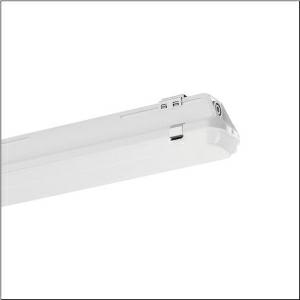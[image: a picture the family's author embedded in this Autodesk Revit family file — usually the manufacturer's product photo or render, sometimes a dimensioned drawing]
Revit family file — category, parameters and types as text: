
# Revit family: monsun_r__11_emergency_51fp207p437l3g_ce37
name_source: partatom
category: Lighting Fixtures
units: mm (PartAtom-declared; Revit-internal decimal feet)

## family parameters
Cut with Voids When Loaded = No
Host = Face
Light Source = No
Part Type = Normal
Room Calculation Point = No
Round Connector Dimension = Use Diameter
Shared = No

## types (1)
- --- (1 x LED, 890 lm, 6.4 W, 4000K)
    Apparent Load = 6 VA
    CIE Flux Codes = 45 75 93 94 100
    Color Rendering = 80
    Color Temperature = 4000K
    Default Elevation = 1800 mm
    Description = Monsun® 11 emergency, damp-proof luminaire, chain hanger, primary optical cover: enclosure, of PC, light emission: direct distribution, primary light characteristic: symmetric, installation type: suspended mounting, surface-mounted, horizontal mounting, vertical mounting, LED, rated luminous flux: 3.990lm, luminous efficacy: 164lm/W, light colour: 840, colour temperature: 4000K, control gear: ON/OFF, with terminal, 4-pole, max. 2.5mm², mains connection: 220..240V, AC, 50/60Hz, rated input power: 28W, control gear: single battery element, battery: LiFePO4, 9Ah, luminaire housing, of glass-fibre reinforced polyester, uncoated, bright grey, incl. chain hanger, length: 1.590mm, width: 90mm, height: 88mm, clip for enclosure, of stainless steel (V2A), ceiling mounting element, of stainless steel (V2A), chain hanger, of stainless steel (V2A), protection rating (complete): IP66, insulation class (complete): insulation class I (protective earthing), certification: CE, UKCA, protection symbol: D, impact resistance: IK08, permissible operating ambient temperature: +5..+35°C, standard: EN 50419, EN 60598-2-1, EN 60598-2-22, contact your sales advisor before using the luminaires in applications with unclear chemical exposure, large temperature fluctuations or condensation-forming humidity, LABS conformity tested according to VDMA 24364:2018-05, no direct snow, no direct sun, no direct rain, for indoor or canopied outdoor use, corresponds to IFS (International Featured Standards) requirements for safety and quality in the food industry, packaging unit: 1 piece
    Height = 89 mm
    Lamp = 1 x LED
    Lamp Light Flux = 890 lm
    Lamp Power = 6.4 W
    Lamp count = 1
    Length = 1590 mm
    Luminous efficacy = 139 lm/W
    Manufacturer = Siteco
    ModVariant = No
    Model = 51FP207P437L3G
    Mounting Place = Ceiling
    Mounting Type = Surface mounted
    Number of Poles = 1
    OnlyDefault = Yes
    Power Factor = 1
    Product Name = Monsun® 11 emergency
    Product group = damp-proof luminaire
    ProductGroupID = 300
    Protection Class = Protection class I
    Protection Degree = IP 66
    RLX_Detail_Level = 1
    RLX_Emergency_Light_Flux = 0 lm
    RLX_Emergency_Type = 0
    RLX_Emergency_Type_DB = No
    RlxData = <blob elided: 88681 chars, md5=a2ae6787>
    Socket = socket
    Standby Power = 0 W
    System Light Flux = 890 lm
    System Power = 6 W
    Type Comments = : emergency light operation: 3 h
    Type Image = l_1349237.jpg
    URL = http://relux.com
    VarID = @adj_018358
    Voltage = 0 V
    Weight = 0.00 kg
    Width = 90 mm

## geometry (parser evidence)
native form markers: Blend x4, Sweep x11
no freeform markers — native parametric forms only
